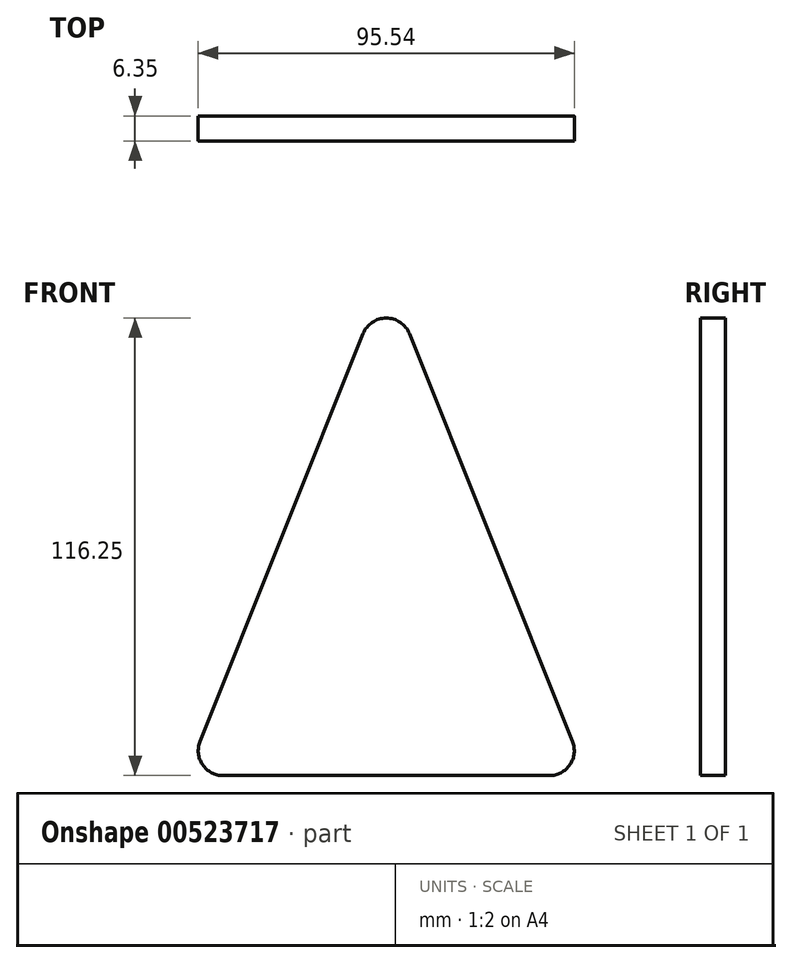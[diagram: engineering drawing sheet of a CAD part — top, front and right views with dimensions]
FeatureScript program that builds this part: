
annotation { "Feature Type Name" : "Feature", "Feature Type Description" : "" }
export const myFeature = defineFeature(function(context is Context, id is Id, definition is map)
    precondition{}
    {
        {
            var Q0;
            Q0=qCreatedBy(makeId("Front.planeOp"),FACE);
            var sketch = newSketch(context, id + "F0", { "sketchPlane" : qUnion([Q0])});
            skLineSegment(sketch, "E0", {"start": v(19.23, 74.2) * mm, "end": v(19.23, -52.8) * mm});
            skLineSegment(sketch, "E1", {"start": v(60.65, -52.8) * mm, "end": v(-22.19, -52.8) * mm});
            skLineSegment(sketch, "E2", {"start": v(25.13, 59.46) * mm, "end": v(66.55, -44.1) * mm});
            skLineSegment(sketch, "E3", {"start": v(13.34, 59.46) * mm, "end": v(-28.08, -44.1) * mm});
            skPoint(sketch, "E4.visualSharp", {"position": v(19.23, 74.2) * mm});
            skArc(sketch, "E4.filletArc", {"start": v(25.13, 59.46) * mm, "mid": v(19.23, 63.45) * mm, "end": v(13.34, 59.46) * mm});
            skPoint(sketch, "E5.visualSharp", {"position": v(70.03, -52.8) * mm});
            skArc(sketch, "E5.filletArc", {"start": v(60.65, -52.8) * mm, "mid": v(65.91, -50.01) * mm, "end": v(66.55, -44.1) * mm});
            skPoint(sketch, "E6.visualSharp", {"position": v(-31.57, -52.8) * mm});
            skArc(sketch, "E6.filletArc", {"start": v(-28.08, -44.1) * mm, "mid": v(-27.45, -50.01) * mm, "end": v(-22.19, -52.8) * mm});
            skSolve(sketch);
        }
        {
            var Q0;
            {var subQ1=sQuery(id+"F0.wireOp",EDGE,"E3");Q0=makeQuery(id+"F0.imprint","IMPRINT",FACE,{"disambiguationData":[TD([[makeQuery(id+"F0.imprint","IMPRINT",EDGE,{"derivedFrom":subQ1}),1.0]])]});}
            var Q1;
            {var subQ0=sQuery(id+"F0.wireOp",EDGE,"E2");Q1=makeQuery(id+"F0.imprint","IMPRINT",FACE,{"disambiguationData":[TD([[makeQuery(id+"F0.imprint","IMPRINT",EDGE,{"derivedFrom":subQ0}),-1.0]])]});}
            extrude(context, id + "F1", {"entities" : qUnion([Q0, Q1]), "depth" : 6.35 * mm, "offsetDistance" : 25.4 * mm});
        }
    });
